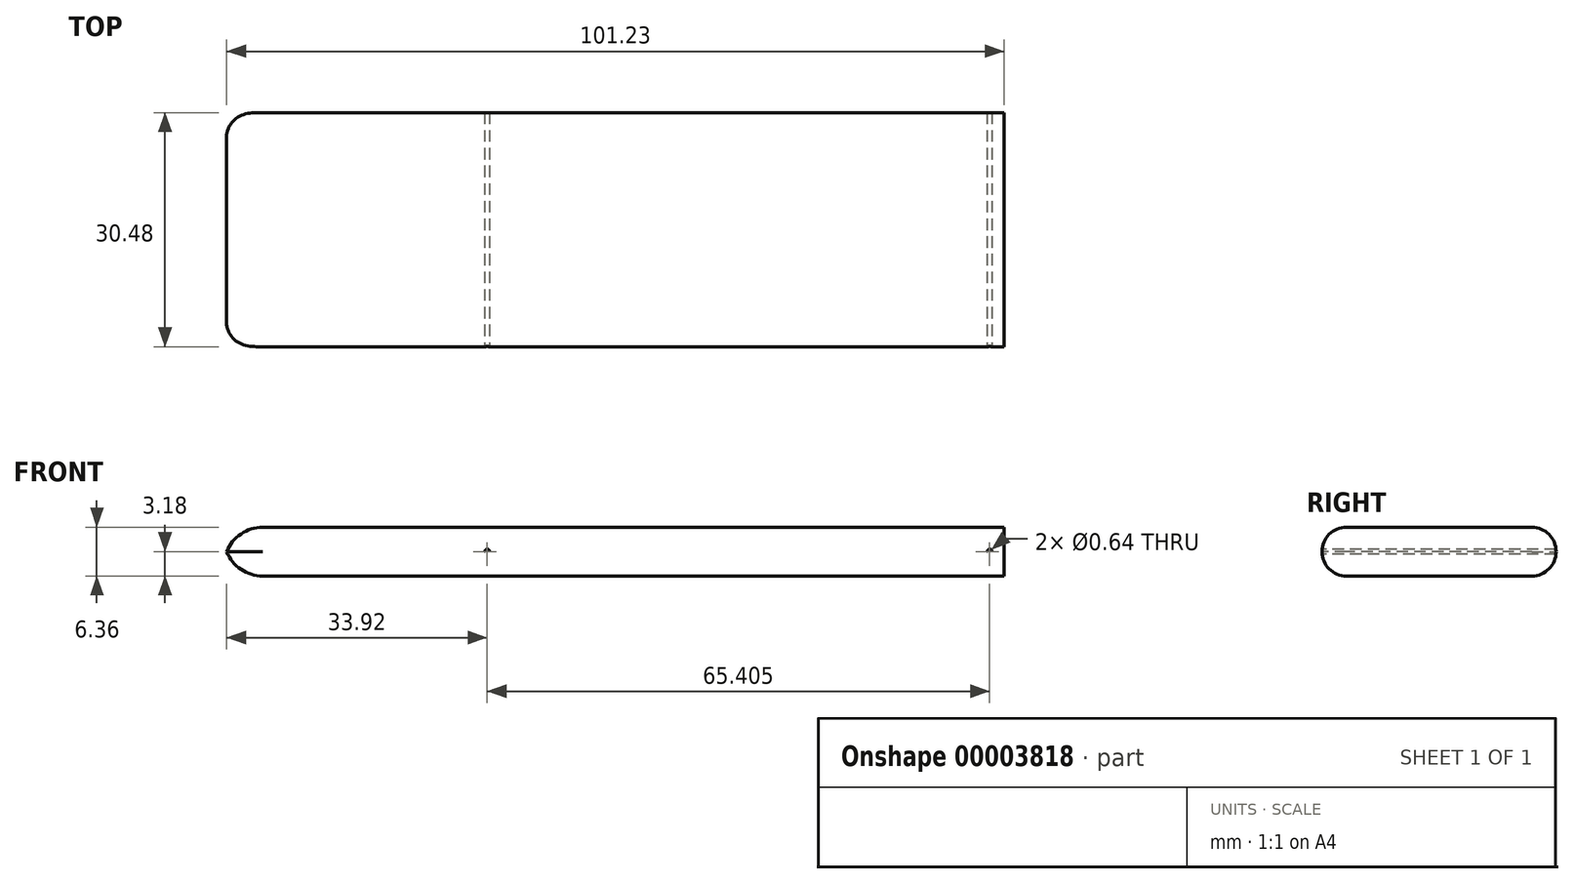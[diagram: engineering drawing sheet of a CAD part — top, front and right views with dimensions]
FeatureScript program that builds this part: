
annotation { "Feature Type Name" : "Feature", "Feature Type Description" : "" }
export const myFeature = defineFeature(function(context is Context, id is Id, definition is map)
    precondition{}
    {
        {
            var Q0;
            Q0=qCreatedBy(makeId("Right.planeOp"),FACE);
            var sketch = newSketch(context, id + "F0", { "sketchPlane" : qUnion([Q0])});
            skLineSegment(sketch, "E0.rect.bottom", {"start": v(15.24, -3.17) * mm, "end": v(-15.24, -3.18) * mm});
            skLineSegment(sketch, "E0.rect.top", {"start": v(15.24, 3.18) * mm, "end": v(-15.24, 3.18) * mm});
            skLineSegment(sketch, "E0.rect.left", {"start": v(15.24, -3.17) * mm, "end": v(15.24, 3.18) * mm});
            skLineSegment(sketch, "E0.rect.right", {"start": v(-15.24, -3.17) * mm, "end": v(-15.24, 3.18) * mm});
            skPoint(sketch, "E0.rect.middle", {"position": v(0, 0) * mm});
            skSolve(sketch);
        }
        {
            var Q0;
            Q0=qCreatedBy(makeId("Front.planeOp"),FACE);
            var sketch = newSketch(context, id + "F1", { "sketchPlane" : qUnion([Q0])});
            skLineSegment(sketch, "E1", {"start": v(0, 0) * mm, "end": v(57.15, 0) * mm});
            skPoint(sketch, "E2.end.orphan", {"position": v(0, 50.8) * mm});
            skSolve(sketch);
        }
        {
            var Q0;
            Q0=makeQuery(id+"F0.imprint","IMPRINT",FACE,{"disambiguationData":[TD([[makeQuery(id+"F0.imprint","IMPRINT",EDGE,{"derivedFrom":sQuery(id+"F0.wireOp",EDGE,"E0.rect.bottom")}),-1.0]])]});
            var Q1;
            Q1=sQuery(id+"F1.wireOp",EDGE,"E1");
            sweep(context, id + "F2", {"profiles" : qUnion([Q0]), "path" : qUnion([Q1])});
        }
        {
            var Q0;
            Q0=makeQuery(id+"F2.opSweep","CAP_FACE",FACE,{"disambiguationData":[OSD([sQuery(id+"F0.wireOp",EDGE,"E0.rect.bottom"),sQuery(id+"F0.wireOp",EDGE,"E0.rect.top"),sQuery(id+"F0.wireOp",EDGE,"E0.rect.left"),sQuery(id+"F0.wireOp",EDGE,"E0.rect.right"),sQuery(id+"F1.wireOp",VERTEX,"E1.end")])],"isStart":false});
            var sketch = newSketch(context, id + "F3", { "sketchPlane" : qUnion([Q0])});
            skLineSegment(sketch, "E3.bottom", {"start": v(15.24, 3.17) * mm, "end": v(-15.24, 3.17) * mm});
            skLineSegment(sketch, "E3.top", {"start": v(15.24, -3.17) * mm, "end": v(-15.24, -3.18) * mm});
            skLineSegment(sketch, "E3.left", {"start": v(-15.24, -3.18) * mm, "end": v(-15.24, 3.17) * mm});
            skLineSegment(sketch, "E3.right", {"start": v(15.24, -3.18) * mm, "end": v(15.24, 3.17) * mm});
            skSolve(sketch);
        }
        {
            var Q0;
            Q0=makeQuery(id+"F3.imprint","IMPRINT",FACE,{"disambiguationData":[TD([[makeQuery(id+"F3.imprint","IMPRINT",EDGE,{"derivedFrom":sQuery(id+"F3.wireOp",EDGE,"E3.bottom")}),1.0]])]});
            extrude(context, id + "F4", {"entities" : qUnion([Q0]), "operationType" : NewBodyOperationType.ADD, "depth" : 12.7 * mm});
        }
        {
            var Q0;
            Q0=makeQuery(id+"F4.boolean.opBoolean","MERGE",FACE,{"derivedFrom":[makeQuery(id+"F2.opSweep","SWEPT_FACE",FACE,{"disambiguationData":[OSD([sQuery(id+"F0.wireOp",EDGE,"E0.rect.right"),sQuery(id+"F1.wireOp",EDGE,"E1")])]}),makeQuery(id+"F4.opExtrude","SWEPT_FACE",FACE,{"disambiguationData":[OSD([sQuery(id+"F3.wireOp",EDGE,"E3.left")])]})]});
            var sketch = newSketch(context, id + "F5", { "sketchPlane" : qUnion([Q0])});
            skCircle(sketch, "E4", {"center": v(2.54, 0) * mm, "radius": 0.32 * mm});
            skSolve(sketch);
        }
        {
            var Q0;
            Q0=makeQuery(id+"F5.imprint","IMPRINT",FACE,{"disambiguationData":[TD([[makeQuery(id+"F5.imprint","IMPRINT",EDGE,{"derivedFrom":sQuery(id+"F5.wireOp",EDGE,"E4")}),1.0]])]});
            extrude(context, id + "F6", {"entities" : qUnion([Q0]), "operationType" : NewBodyOperationType.REMOVE, "endBound" : BoundingType.THROUGH_ALL, "oppositeDirection" : true, "depth" : 25.4 * mm});
        }
        {
            var Q0;
            Q0=makeQuery(id+"F4.boolean.opBoolean","MERGE",FACE,{"derivedFrom":[makeQuery(id+"F2.opSweep","SWEPT_FACE",FACE,{"disambiguationData":[OSD([sQuery(id+"F0.wireOp",EDGE,"E0.rect.right"),sQuery(id+"F1.wireOp",EDGE,"E1")])]}),makeQuery(id+"F4.opExtrude","SWEPT_FACE",FACE,{"disambiguationData":[OSD([sQuery(id+"F3.wireOp",EDGE,"E3.left")])]})]});
            var sketch = newSketch(context, id + "F7", { "sketchPlane" : qUnion([Q0])});
            skCircle(sketch, "E5", {"center": v(67.95, 0) * mm, "radius": 0.32 * mm});
            skLineSegment(sketch, "E6", {"start": v(69.85, 0) * mm, "end": v(75.98, 0) * mm, "construction": true});
            skSolve(sketch);
        }
        {
            var Q0;
            Q0=makeQuery(id+"F7.imprint","IMPRINT",FACE,{"disambiguationData":[TD([[makeQuery(id+"F7.imprint","IMPRINT",EDGE,{"derivedFrom":sQuery(id+"F7.wireOp",EDGE,"E5")}),1.0]])]});
            extrude(context, id + "F8", {"entities" : qUnion([Q0]), "operationType" : NewBodyOperationType.REMOVE, "endBound" : BoundingType.THROUGH_ALL, "oppositeDirection" : true, "depth" : 25.4 * mm});
        }
        {
            var Q0;
            Q0=makeQuery(id+"F2.opSweep","CAP_FACE",FACE,{"disambiguationData":[OSD([sQuery(id+"F0.wireOp",EDGE,"E0.rect.bottom"),sQuery(id+"F0.wireOp",EDGE,"E0.rect.top"),sQuery(id+"F0.wireOp",EDGE,"E0.rect.left"),sQuery(id+"F0.wireOp",EDGE,"E0.rect.right"),sQuery(id+"F1.wireOp",VERTEX,"E1.start")])],"isStart":true});
            var sketch = newSketch(context, id + "F9", { "sketchPlane" : qUnion([Q0])});
            skLineSegment(sketch, "E7.bottom", {"start": v(15.24, -3.18) * mm, "end": v(-15.24, -3.18) * mm});
            skLineSegment(sketch, "E7.top", {"start": v(15.24, 3.18) * mm, "end": v(-15.24, 3.18) * mm});
            skLineSegment(sketch, "E7.left", {"start": v(15.24, -3.18) * mm, "end": v(15.24, 3.18) * mm});
            skLineSegment(sketch, "E7.right", {"start": v(-15.24, -3.18) * mm, "end": v(-15.24, 3.18) * mm});
            skSolve(sketch);
        }
        {
            var Q0;
            Q0=makeQuery(id+"F9.imprint","IMPRINT",FACE,{"disambiguationData":[TD([[makeQuery(id+"F9.imprint","IMPRINT",EDGE,{"derivedFrom":sQuery(id+"F9.wireOp",EDGE,"E7.bottom")}),-1.0]])]});
            extrude(context, id + "F10", {"entities" : qUnion([Q0]), "operationType" : NewBodyOperationType.ADD, "depth" : 31.75 * mm});
        }
        {
            var Q0;
            Q0=makeQuery(id+"F10.opExtrude","CAP_EDGE",EDGE,{"disambiguationData":[OSD([sQuery(id+"F9.wireOp",EDGE,"E7.top")])],"isStart":false});
            var Q1;
            Q1=makeQuery(id+"F10.opExtrude","CAP_EDGE",EDGE,{"disambiguationData":[OSD([sQuery(id+"F9.wireOp",EDGE,"E7.bottom")])],"isStart":false});
            fillet(context, id + "F11", {"entities" : qUnion([Q0, Q1]), "radius" : 5.08 * mm, "tangentPropagation" : true, "allowEdgeOverflow" : false});
        }
        {
            var Q0;
            Q0=makeQuery(id+"F10.boolean.opBoolean","MERGE",EDGE,{"derivedFrom":[makeQuery(id+"F4.boolean.opBoolean","MERGE",EDGE,{"derivedFrom":[makeQuery(id+"F2.opSweep","SWEPT_EDGE",EDGE,{"disambiguationData":[OSD([sQuery(id+"F0.wireOp",EDGE,"E0.rect.bottom"),sQuery(id+"F0.wireOp",EDGE,"E0.rect.left"),sQuery(id+"F1.wireOp",EDGE,"E1")])]}),makeQuery(id+"F4.opExtrude","SWEPT_EDGE",EDGE,{"disambiguationData":[OSD([sQuery(id+"F3.wireOp",EDGE,"E3.top"),sQuery(id+"F3.wireOp",EDGE,"E3.right")])]})]}),makeQuery(id+"F10.opExtrude","SWEPT_EDGE",EDGE,{"disambiguationData":[OSD([sQuery(id+"F9.wireOp",EDGE,"E7.bottom"),sQuery(id+"F9.wireOp",EDGE,"E7.right")])]})]});
            var Q1;
            Q1=makeQuery(id+"F10.boolean.opBoolean","MERGE",EDGE,{"derivedFrom":[makeQuery(id+"F4.boolean.opBoolean","MERGE",EDGE,{"derivedFrom":[makeQuery(id+"F2.opSweep","SWEPT_EDGE",EDGE,{"disambiguationData":[OSD([sQuery(id+"F0.wireOp",EDGE,"E0.rect.bottom"),sQuery(id+"F0.wireOp",EDGE,"E0.rect.left"),sQuery(id+"F1.wireOp",EDGE,"E1")])]}),makeQuery(id+"F4.opExtrude","SWEPT_EDGE",EDGE,{"disambiguationData":[OSD([sQuery(id+"F3.wireOp",EDGE,"E3.top"),sQuery(id+"F3.wireOp",EDGE,"E3.right")])]})]}),makeQuery(id+"F10.opExtrude","SWEPT_EDGE",EDGE,{"disambiguationData":[OSD([sQuery(id+"F9.wireOp",EDGE,"E7.bottom"),sQuery(id+"F9.wireOp",EDGE,"E7.right")])]})]});
            var Q2;
            Q2=makeQuery(id+"F10.boolean.opBoolean","MERGE",EDGE,{"derivedFrom":[makeQuery(id+"F4.boolean.opBoolean","MERGE",EDGE,{"derivedFrom":[makeQuery(id+"F2.opSweep","SWEPT_EDGE",EDGE,{"disambiguationData":[OSD([sQuery(id+"F0.wireOp",EDGE,"E0.rect.top"),sQuery(id+"F0.wireOp",EDGE,"E0.rect.right"),sQuery(id+"F1.wireOp",EDGE,"E1")])]}),makeQuery(id+"F4.opExtrude","SWEPT_EDGE",EDGE,{"disambiguationData":[OSD([sQuery(id+"F3.wireOp",EDGE,"E3.bottom"),sQuery(id+"F3.wireOp",EDGE,"E3.left")])]})]}),makeQuery(id+"F10.opExtrude","SWEPT_EDGE",EDGE,{"disambiguationData":[OSD([sQuery(id+"F9.wireOp",EDGE,"E7.top"),sQuery(id+"F9.wireOp",EDGE,"E7.left")])]})]});
            var Q3;
            Q3=makeQuery(id+"F10.boolean.opBoolean","MERGE",EDGE,{"derivedFrom":[makeQuery(id+"F4.boolean.opBoolean","MERGE",EDGE,{"derivedFrom":[makeQuery(id+"F2.opSweep","SWEPT_EDGE",EDGE,{"disambiguationData":[OSD([sQuery(id+"F0.wireOp",EDGE,"E0.rect.top"),sQuery(id+"F0.wireOp",EDGE,"E0.rect.left"),sQuery(id+"F1.wireOp",EDGE,"E1")])]}),makeQuery(id+"F4.opExtrude","SWEPT_EDGE",EDGE,{"disambiguationData":[OSD([sQuery(id+"F3.wireOp",EDGE,"E3.bottom"),sQuery(id+"F3.wireOp",EDGE,"E3.right")])]})]}),makeQuery(id+"F10.opExtrude","SWEPT_EDGE",EDGE,{"disambiguationData":[OSD([sQuery(id+"F9.wireOp",EDGE,"E7.top"),sQuery(id+"F9.wireOp",EDGE,"E7.right")])]})]});
            var Q4;
            Q4=makeQuery(id+"F10.boolean.opBoolean","MERGE",EDGE,{"derivedFrom":[makeQuery(id+"F4.boolean.opBoolean","MERGE",EDGE,{"derivedFrom":[makeQuery(id+"F2.opSweep","SWEPT_EDGE",EDGE,{"disambiguationData":[OSD([sQuery(id+"F0.wireOp",EDGE,"E0.rect.bottom"),sQuery(id+"F0.wireOp",EDGE,"E0.rect.right"),sQuery(id+"F1.wireOp",EDGE,"E1")])]}),makeQuery(id+"F4.opExtrude","SWEPT_EDGE",EDGE,{"disambiguationData":[OSD([sQuery(id+"F3.wireOp",EDGE,"E3.top"),sQuery(id+"F3.wireOp",EDGE,"E3.left")])]})]}),makeQuery(id+"F10.opExtrude","SWEPT_EDGE",EDGE,{"disambiguationData":[OSD([sQuery(id+"F9.wireOp",EDGE,"E7.bottom"),sQuery(id+"F9.wireOp",EDGE,"E7.left")])]})]});
            fillet(context, id + "F12", {"entities" : qUnion([Q0, Q1, Q2, Q3, Q4]), "radius" : 3.17 * mm, "tangentPropagation" : true, "allowEdgeOverflow" : false});
        }
    });
